# Revit family: FU_Chair_Sandler_Ithaca 1-1
name_source: partatom
category: Furniture
units: mm (PartAtom-declared; Revit-internal decimal feet)

## family parameters
Always vertical = Yes
Cut with Voids When Loaded = No
OmniClass Number = 23.40.20.00
OmniClass Title = General Furniture and Specialties
Render Appearance Source = Family Geometry
Room Calculation Point = No
Shared = No
Work Plane-Based = No

## types (1)
- Ithaca 1.1
    Default Elevation = 0 mm  [stored 0 ft]
    Depth = 535 mm  [stored 1.75525 ft]
    Description = Outdoor polypropylene side chair. Stackable and reinforced with fiberglass for extra durability.
    Height = 795 mm  [stored 2.60827 ft]
    Model = Ithaca 1.1
    URL = https://www.sandlerseating.com
    Width = 563 mm  [stored 1.84711 ft]

note: [stored X ft] marks values corroborated as IEEE doubles in the binary element streams (Revit-internal decimal feet)

## geometry (parser evidence)
native form markers: Sweep x6
no freeform markers — native parametric forms only
